# Revit family: JLR_BossDesign_Stng_Toto_LowBack
name_source: partatom
category: Furniture
revit_build: Autodesk Revit 2015 (Build: 20140903_1530(x64)
units: mm (PartAtom-declared; Revit-internal decimal feet)

## types (2) — shared parameters
Assembly Code = E2020200
AssetType = Movable
BIMObjectName = JLR_BossDesign_Seating_Toto_LowBack
Category = Pr_40_50_12 : Chairs, seats and benches
Color = Brown
Description = Toto Wooden Leg Chair
DurationUnit = year
ExpectedLife = 5
Finish = Fabric
IfcExportAs = IfcFurnishingElementType
IfcExportType = CHAIR
Keynote = Pr_40_50_12
MainColor = Brown
ManufacturerName = Boss Design
ManufacturerURL = www.bossdesign.com
ModelReference = Toto Wooden Leg Chair
NBSDescription = Seating
NBSReference = 45-35-72/352
Name = Seating_Toto_LowBack_BossDesign
NominalHeight = 745 mm  [stored 2.44423 ft]
NominalLength = 620 mm  [stored 2.03412 ft]
NominalWidth = 550 mm
ProductInformation = www.bossdesign.com/product-list/toto/
Shape = Rectangular
Size = 620 x 550 x 745mm
URL = www.bossdesign.com
Uniclass2015Code = Pr_40_50_12
Uniclass2015Title = Chairs, seats and benches
Uniclass2015Version = Products v1.10
Version = 1
WarrantyDescription = Structural Warranty Excludes Foams and Fabrics
WarrantyDurationLabor = 5
WarrantyDurationParts = 5
WarrantyDurationUnit = year

## per-type parameters (varying)
| type | FrameMaterial | Model | ModelNumber | SeatBackMaterial | SeatMaterial |
| Toto Wooden Leg Chair 026 B | BDG_Generic_Metal_White | BOS-JLR-F-026 B | BOS-JLR-F-026 B | BDG_JLR_Fabric_HEMP_Harvest07284 | BDG_JLR_Fabric_HEMP_Furrow07271 |
| Toto Wooden Leg Chair 229 | BDG_Generic_Metal_Black | BOS-JLR-F-0229 | BOS-JLR-F-0229 | BDG_JLR_Fabric_HEMP_Sickle | BDG_JLR_Fabric_HEMP_Harvest07284 |

note: [stored X ft] marks values corroborated as IEEE doubles in the binary element streams (Revit-internal decimal feet)

## geometry (parser evidence)
native form markers: Sweep x2
no freeform markers — native parametric forms only
